# Revit family: Haworth_Maari_Chair_StarBase_AP_PRELIMINARY
name_source: partatom
category: Furniture
units: mm (PartAtom-declared; Revit-internal decimal feet)

## family parameters
Always vertical = Yes
Cut with Voids When Loaded = No
OmniClass Number = 23.40.70.14.64.21
OmniClass Title = Systems Furniture
Room Calculation Point = No
Shared = No
Work Plane-Based = No

## types (4) — shared parameters
Arm Cap Finish = Haworth _ Polymer _ Undecided
Assembly Code = E2020200
Description = Haworth - Maari - Chair - Star Base
Manufacturer = Haworth
Model = SEMIGX
Revision Number = 2
Seat Pan Finish = Haworth _ Paint _ Black
Size = Verify Final Dim. w/ Haworth
URL = https://www.haworth.com
URL - Product = https://www.haworth.com
Warranty = http://www.haworth.com

## per-type parameters (varying)
| type | Actual Depth | Actual Height | Actual Width | Five Star Base | Four Star Base | With Arms |
| Four Star Base - With Arms | 648 mm | 864 mm | 546 mm | No | Yes | Yes |
| Five Star Base - With Arms | 724 mm | 813 mm | 724 mm | Yes | No | Yes |
| Five Star Base - No Arms | 724 mm | 813 mm | 724 mm | Yes | No | No |
| Four Star Base - No Arms | 648 mm | 864 mm | 546 mm | No | Yes | No |

## geometry (parser evidence)
native form markers: Sweep x14
no freeform markers — native parametric forms only
